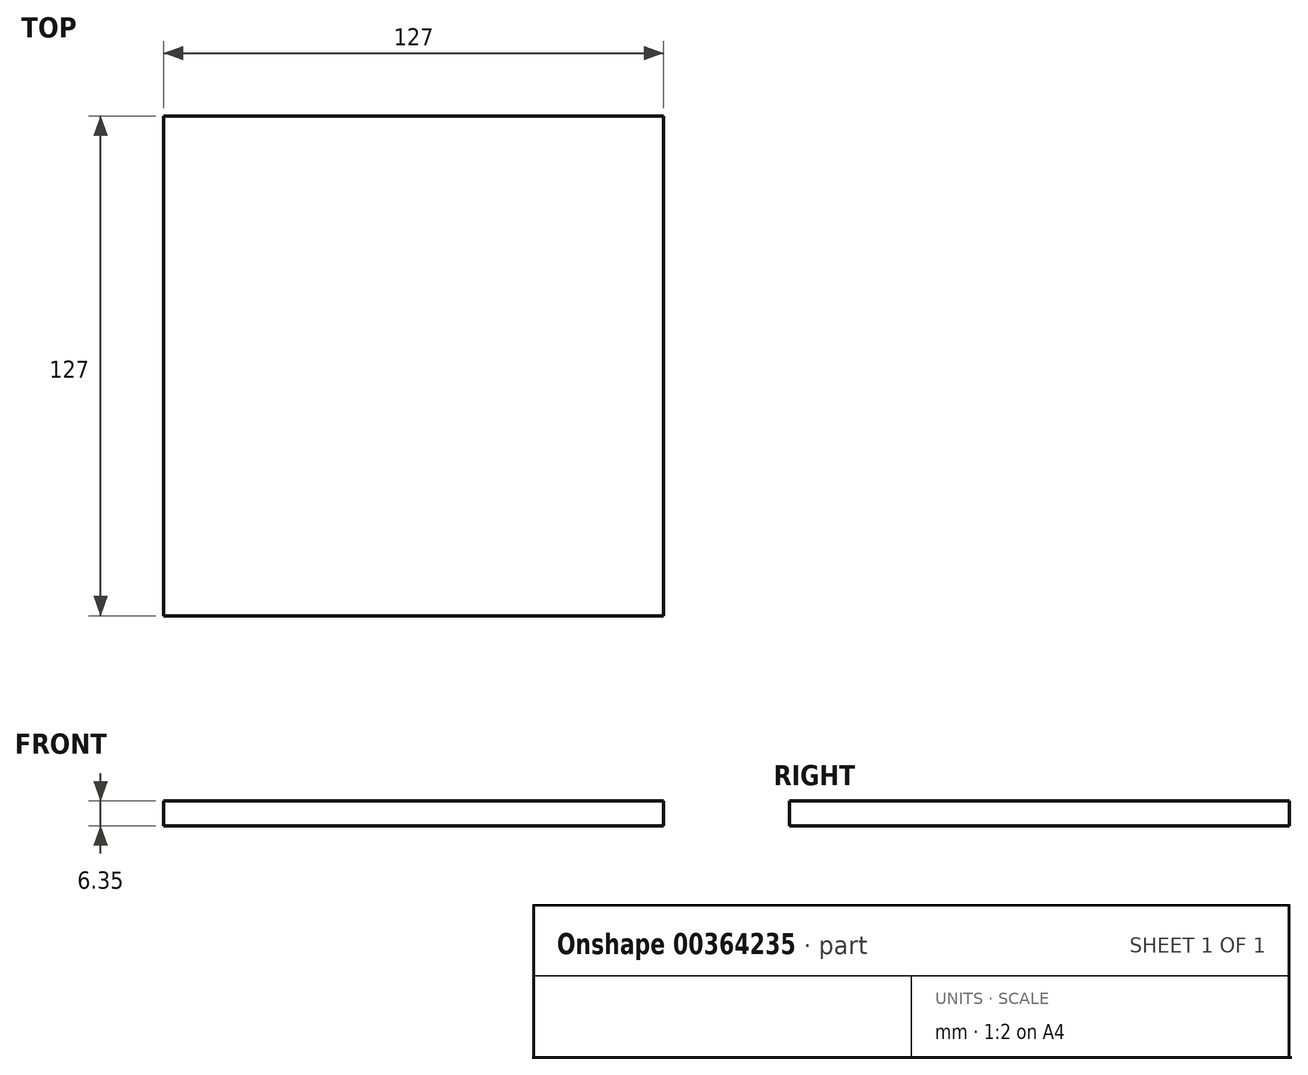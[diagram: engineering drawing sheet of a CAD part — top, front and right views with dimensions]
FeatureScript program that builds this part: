
annotation { "Feature Type Name" : "Feature", "Feature Type Description" : "" }
export const myFeature = defineFeature(function(context is Context, id is Id, definition is map)
    precondition{}
    {
        {
            var Q0;
            Q0=qCreatedBy(makeId("Top.planeOp"),FACE);
            var sketch = newSketch(context, id + "F0", { "sketchPlane" : qUnion([Q0])});
            skLineSegment(sketch, "E0.bottom", {"start": v(0, 0) * mm, "end": v(-127, 0) * mm});
            skLineSegment(sketch, "E0.top", {"start": v(0, -127) * mm, "end": v(-127, -127) * mm});
            skLineSegment(sketch, "E0.left", {"start": v(0, 0) * mm, "end": v(0, -127) * mm});
            skLineSegment(sketch, "E0.right", {"start": v(-127, 0) * mm, "end": v(-127, -127) * mm});
            skSolve(sketch);
        }
        {
            var Q0;
            Q0 = qSketchRegion(id + "F0", true);
            extrude(context, id + "F1", {"entities" : qUnion([Q0]), "depth" : 6.35 * mm});
        }
    });
